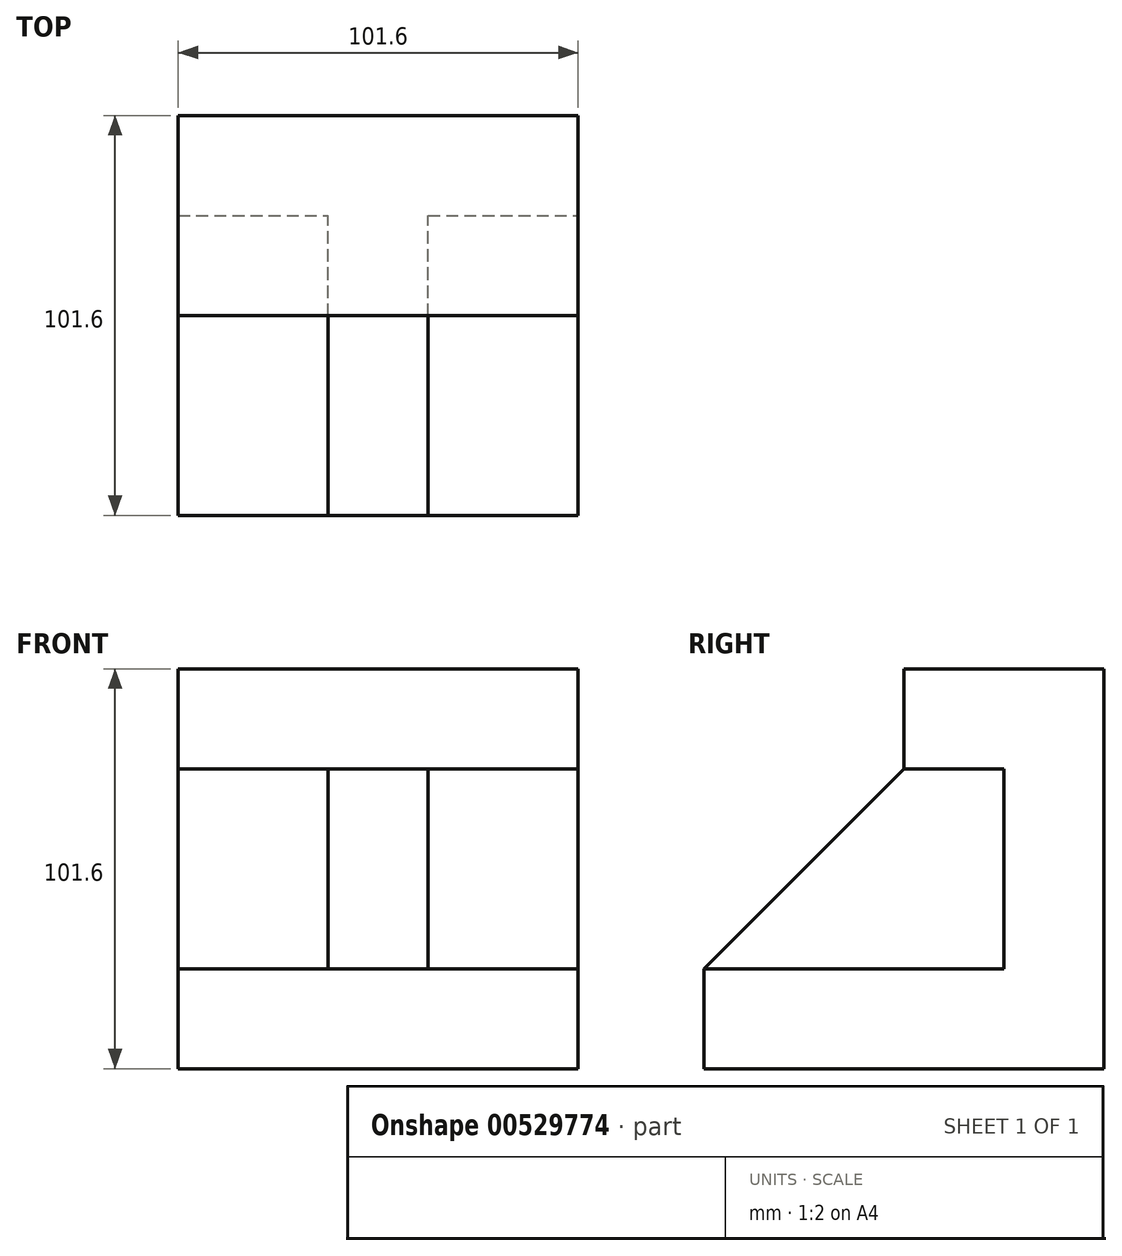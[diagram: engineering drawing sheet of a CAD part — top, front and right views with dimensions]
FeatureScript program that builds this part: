
annotation { "Feature Type Name" : "Feature", "Feature Type Description" : "" }
export const myFeature = defineFeature(function(context is Context, id is Id, definition is map)
    precondition{}
    {
        {
            var Q0;
            Q0=qCreatedBy(makeId("Front.planeOp"),FACE);
            var sketch = newSketch(context, id + "F0", { "sketchPlane" : qUnion([Q0])});
            skLineSegment(sketch, "E0.bottom", {"start": v(-183.93, -102.86) * mm, "end": v(-82.33, -102.86) * mm});
            skLineSegment(sketch, "E0.top", {"start": v(-183.93, -1.26) * mm, "end": v(-82.33, -1.26) * mm});
            skLineSegment(sketch, "E0.left", {"start": v(-183.93, -102.86) * mm, "end": v(-183.93, -1.26) * mm});
            skLineSegment(sketch, "E0.right", {"start": v(-82.33, -102.86) * mm, "end": v(-82.33, -1.26) * mm});
            skSolve(sketch);
        }
        {
            var Q0;
            Q0=makeQuery(id+"F0.imprint","IMPRINT",FACE,{"disambiguationData":[TD([[makeQuery(id+"F0.imprint","IMPRINT",EDGE,{"derivedFrom":sQuery(id+"F0.wireOp",EDGE,"E0.bottom")}),1.0]])]});
            extrude(context, id + "F1", {"entities" : qUnion([Q0]), "depth" : 101.6 * mm, "offsetDistance" : 25.4 * mm});
        }
        {
            var Q0;
            Q0=makeQuery(id+"F1.opExtrude","CAP_FACE",FACE,{"disambiguationData":[OSD([sQuery(id+"F0.wireOp",EDGE,"E0.bottom"),sQuery(id+"F0.wireOp",EDGE,"E0.top"),sQuery(id+"F0.wireOp",EDGE,"E0.left"),sQuery(id+"F0.wireOp",EDGE,"E0.right")])],"isStart":false});
            var sketch = newSketch(context, id + "F2", { "sketchPlane" : qUnion([Q0])});
            skLineSegment(sketch, "E1.bottom", {"start": v(-183.93, -1.26) * mm, "end": v(-82.33, -1.26) * mm});
            skLineSegment(sketch, "E1.top", {"start": v(-183.93, -26.66) * mm, "end": v(-82.33, -26.66) * mm});
            skLineSegment(sketch, "E1.left", {"start": v(-183.93, -1.26) * mm, "end": v(-183.93, -26.66) * mm});
            skLineSegment(sketch, "E1.right", {"start": v(-82.33, -1.26) * mm, "end": v(-82.33, -26.66) * mm});
            skSolve(sketch);
        }
        {
            var Q0;
            {var subQ0=sQuery(id+"F2.wireOp",EDGE,"E1.top");Q0=makeQuery(id+"F2.imprint","IMPRINT",FACE,{"disambiguationData":[TD([[makeQuery(id+"F2.imprint","IMPRINT",EDGE,{"derivedFrom":subQ0}),-1.0]])]});}
            extrude(context, id + "F3", {"entities" : qUnion([Q0]), "operationType" : NewBodyOperationType.REMOVE, "oppositeDirection" : true, "depth" : 76.2 * mm, "offsetDistance" : 25.4 * mm});
        }
        {
            var Q0;
            Q0=makeQuery(id+"F3.boolean.opBoolean","COPY",FACE,{"derivedFrom":makeQuery(id+"F3.opExtrude","CAP_FACE",FACE,{"disambiguationData":[OSD([sQuery(id+"F0.wireOp",EDGE,"E0.bottom"),sQuery(id+"F0.wireOp",EDGE,"E0.left"),sQuery(id+"F0.wireOp",EDGE,"E0.right"),sQuery(id+"F2.wireOp",EDGE,"E1.top")])],"isStart":false})});
            var sketch = newSketch(context, id + "F4", { "sketchPlane" : qUnion([Q0])});
            skLineSegment(sketch, "E2.bottom", {"start": v(-183.93, -102.86) * mm, "end": v(-82.33, -102.86) * mm});
            skLineSegment(sketch, "E2.top", {"start": v(-183.93, -77.46) * mm, "end": v(-82.33, -77.46) * mm});
            skLineSegment(sketch, "E2.left", {"start": v(-183.93, -102.86) * mm, "end": v(-183.93, -77.46) * mm});
            skLineSegment(sketch, "E2.right", {"start": v(-82.33, -102.86) * mm, "end": v(-82.33, -77.46) * mm});
            skSolve(sketch);
        }
        {
            var Q0;
            Q0=makeQuery(id+"F4.imprint","IMPRINT",FACE,{"disambiguationData":[TD([[makeQuery(id+"F4.imprint","IMPRINT",EDGE,{"derivedFrom":sQuery(id+"F4.wireOp",EDGE,"E2.bottom")}),1.0]])]});
            extrude(context, id + "F5", {"entities" : qUnion([Q0]), "operationType" : NewBodyOperationType.ADD, "depth" : 76.2 * mm, "offsetDistance" : 25.4 * mm});
        }
        {
            var Q0;
            Q0=makeQuery(id+"F1.opExtrude","CAP_FACE",FACE,{"disambiguationData":[OSD([sQuery(id+"F0.wireOp",EDGE,"E0.bottom"),sQuery(id+"F0.wireOp",EDGE,"E0.top"),sQuery(id+"F0.wireOp",EDGE,"E0.left"),sQuery(id+"F0.wireOp",EDGE,"E0.right")])],"isStart":false});
            extrude(context, id + "F6", {"entities" : qUnion([Q0]), "operationType" : NewBodyOperationType.REMOVE, "oppositeDirection" : true, "depth" : 50.8 * mm, "offsetDistance" : 25.4 * mm});
        }
        {
            var Q0;
            Q0=makeQuery(id+"F3.boolean.opBoolean","COPY",FACE,{"derivedFrom":makeQuery(id+"F3.opExtrude","CAP_FACE",FACE,{"disambiguationData":[OSD([sQuery(id+"F0.wireOp",EDGE,"E0.bottom"),sQuery(id+"F0.wireOp",EDGE,"E0.left"),sQuery(id+"F0.wireOp",EDGE,"E0.right"),sQuery(id+"F2.wireOp",EDGE,"E1.top")])],"isStart":false})});
            var sketch = newSketch(context, id + "F7", { "sketchPlane" : qUnion([Q0])});
            skLineSegment(sketch, "E3.bottom", {"start": v(-183.93, -77.46) * mm, "end": v(-145.83, -77.46) * mm});
            skLineSegment(sketch, "E3.top", {"start": v(-183.93, -26.66) * mm, "end": v(-145.83, -26.66) * mm});
            skLineSegment(sketch, "E3.left", {"start": v(-183.93, -77.46) * mm, "end": v(-183.93, -26.66) * mm});
            skLineSegment(sketch, "E3.right", {"start": v(-145.83, -77.46) * mm, "end": v(-145.83, -26.66) * mm});
            skLineSegment(sketch, "E4.bottom", {"start": v(-82.33, -26.66) * mm, "end": v(-120.43, -26.66) * mm});
            skLineSegment(sketch, "E4.top", {"start": v(-82.33, -77.46) * mm, "end": v(-120.43, -77.46) * mm});
            skLineSegment(sketch, "E4.left", {"start": v(-82.33, -26.66) * mm, "end": v(-82.33, -77.46) * mm});
            skLineSegment(sketch, "E4.right", {"start": v(-120.43, -26.66) * mm, "end": v(-120.43, -77.46) * mm});
            skSolve(sketch);
        }
        {
            var Q0;
            {var subQ0=sQuery(id+"F7.wireOp",EDGE,"E3.right");Q0=makeQuery(id+"F7.imprint","IMPRINT",FACE,{"disambiguationData":[TD([[makeQuery(id+"F7.imprint","IMPRINT",EDGE,{"derivedFrom":subQ0}),-1.0]])]});}
            extrude(context, id + "F8", {"entities" : qUnion([Q0]), "operationType" : NewBodyOperationType.ADD, "depth" : 76.2 * mm, "offsetDistance" : 25.4 * mm});
        }
        {
            var Q0;
            Q0=makeQuery(id+"F8.opExtrude","SWEPT_FACE",FACE,{"disambiguationData":[OSD([sQuery(id+"F7.wireOp",EDGE,"E4.right")])]});
            var sketch = newSketch(context, id + "F9", { "sketchPlane" : qUnion([Q0])});
            skLineSegment(sketch, "E5", {"start": v(-101.6, -77.46) * mm, "end": v(-50.8, -26.66) * mm});
            skLineSegment(sketch, "E6", {"start": v(-50.8, -26.66) * mm, "end": v(-101.6, -26.66) * mm});
            skLineSegment(sketch, "E7", {"start": v(-101.6, -26.66) * mm, "end": v(-101.6, -77.46) * mm});
            skSolve(sketch);
        }
        {
            var Q0;
            Q0=makeQuery(id+"F9.imprint","IMPRINT",FACE,{"disambiguationData":[TD([[makeQuery(id+"F9.imprint","IMPRINT",EDGE,{"derivedFrom":sQuery(id+"F9.wireOp",EDGE,"E5")}),1.0]])]});
            extrude(context, id + "F10", {"entities" : qUnion([Q0]), "operationType" : NewBodyOperationType.REMOVE, "oppositeDirection" : true, "depth" : 25.4 * mm, "offsetDistance" : 25.4 * mm});
        }
    });
